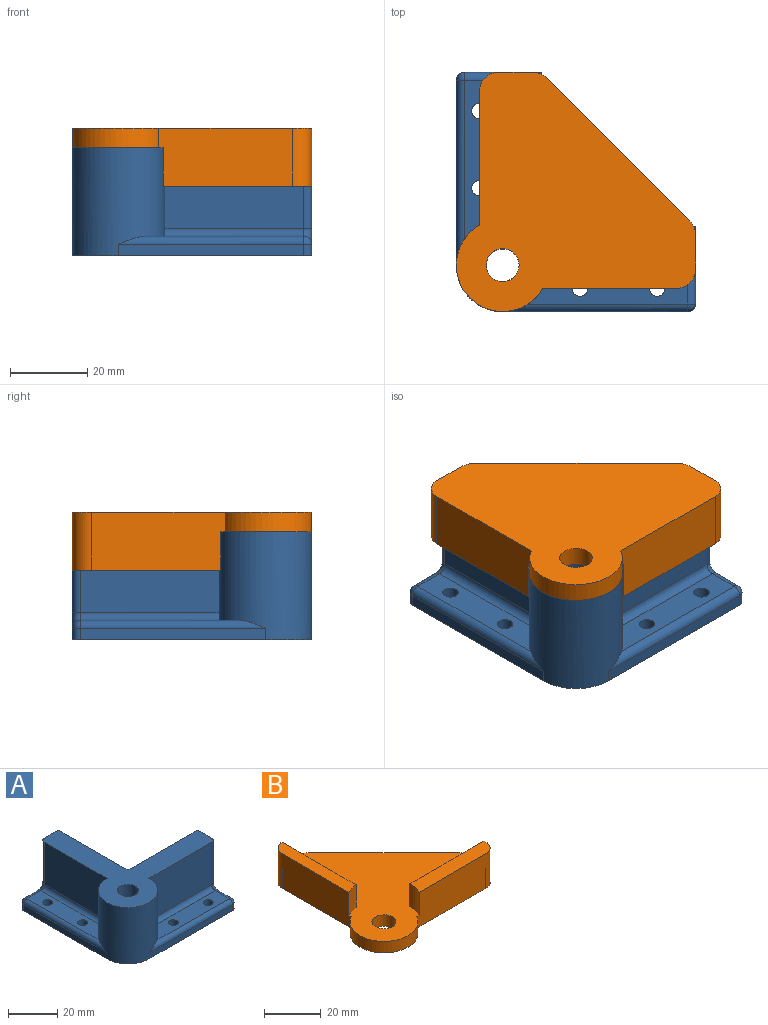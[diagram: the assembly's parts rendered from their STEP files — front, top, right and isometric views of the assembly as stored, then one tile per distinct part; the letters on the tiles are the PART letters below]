
ASSEMBLY  parts=2 mates=1
PART A: 40 faces, bbox 62x62x28 mm
  f0: cylinder r=12mm len=28mm, axis (0,0,-1), area 1404mm2, adj f1,f2,f7,f8,f11,f12,f13,f16
  f1: plane 36x21mm, normal (-1,0,0), area 756mm2, adj f0,f7,f28,f31
  f2: plane 36x21mm, normal (0,-1,0), area 756mm2, adj f0,f7,f32,f33
  f3: plane 28x20mm, normal (1,0,0), area 263.4mm2, adj f4,f7,f8,f33,f34,f36,f38
  f4: plane 38x28mm, normal (0,1,0), area 1064mm2, adj f3,f7,f8,f39
  f5: plane 38x28mm, normal (1,0,0), area 1064mm2, adj f6,f7,f8,f39
  f6: plane 28x20mm, normal (0,1,0), area 263.4mm2, adj f5,f7,f8,f26,f29,f30,f31
  f7: plane 62x62mm, normal (0,0,1), area 1181.7mm2, adj f0,f1,f2,f3,f4,f5,f6,f17
  f8: plane 62x62mm, normal (0,0,-1), area 2015.8mm2, adj f0,f3,f4,f5,f6,f9,f10,f11
  f9: cylinder r=2mm len=5mm, axis (0,0,-1), area 62.8mm2, adj f8,f12
  f10: cylinder r=2mm len=5mm, axis (0,0,-1), area 62.8mm2, adj f8,f12
  f11: plane 48x3mm, normal (-1,0,0), area 144mm2, adj f0,f8,f25,f26
  f12: plane 41.37x8mm, normal (0,0,1), area 278.7mm2, adj f0,f9,f10,f25,f28,f29
  f13: plane 48x3mm, normal (0,-1,0), area 144mm2, adj f0,f8,f35,f38
  f14: cylinder r=2mm len=5mm, axis (0,0,-1), area 62.8mm2, adj f8,f16
  f15: cylinder r=2mm len=5mm, axis (0,0,-1), area 62.8mm2, adj f8,f16
  f16: plane 41.37x8mm, normal (0,0,1), area 278.7mm2, adj f0,f14,f15,f32,f35,f36
  f17: cylinder r=4.25mm len=21mm, axis (0,0,-1), area 560.8mm2, adj f7,f24
  f18: plane 7.26x7mm, normal (-0.25,0.97,0), area 52.5mm2, adj f8,f19,f23,f24
  f19: plane 7.23x7mm, normal (-0.96,0.27,0), area 52.5mm2, adj f8,f18,f20,f24
  f20: plane 7x5.34mm, normal (-0.71,-0.7,0), area 52.5mm2, adj f8,f19,f21,f24
  f21: plane 7.26x7mm, normal (0.25,-0.97,0), area 52.5mm2, adj f8,f20,f22,f24
  f22: plane 7.23x7mm, normal (0.96,-0.27,0), area 52.5mm2, adj f8,f21,f23,f24
  f23: plane 7x5.34mm, normal (0.71,0.7,0), area 52.5mm2, adj f8,f18,f22,f24
  f24: plane 14.52x14.46mm, normal (0,0,-1), area 89.4mm2, adj f17,f18,f19,f20,f21,f22,f23
  f25: cylinder r=2mm len=48mm, axis (0,1,0), area 139.6mm2, adj f0,f11,f12,f27
  f26: cylinder r=2mm len=3mm, axis (0,0,-1), area 9.4mm2, adj f6,f8,f11,f27
  f27: sphere r=2mm, area 6.3mm2, adj f25,f26,f29
  f28: cylinder r=2mm len=36.17mm, axis (0,-1,0), area 113.4mm2, adj f0,f1,f12,f30
  f29: cylinder r=2mm len=8mm, axis (1,0,0), area 25.1mm2, adj f6,f12,f27,f30
  f30: torus R=4mm, axis (0,1,0), area 13.5mm2, adj f6,f28,f29,f31
  f31: cylinder r=2mm len=21mm, axis (0,0,-1), area 66mm2, adj f1,f6,f7,f30
  f32: cylinder r=2mm len=36.17mm, axis (1,0,0), area 113.4mm2, adj f0,f2,f16,f34
  f33: cylinder r=2mm len=21mm, axis (0,0,-1), area 66mm2, adj f2,f3,f7,f34
  f34: torus R=4mm, axis (1,0,0), area 13.5mm2, adj f3,f32,f33,f36
  f35: cylinder r=2mm len=48mm, axis (-1,0,0), area 139.6mm2, adj f0,f13,f16,f37
  f36: cylinder r=2mm len=8mm, axis (0,1,0), area 25.1mm2, adj f3,f16,f34,f37
  f37: sphere r=2mm, area 6.3mm2, adj f35,f36,f38
  f38: cylinder r=2mm len=3mm, axis (0,0,1), area 9.4mm2, adj f3,f8,f13,f37
  f39: cylinder r=2mm len=28mm, axis (0,0,1), area 88mm2, adj f4,f5,f7,f8
PART B: 19 faces, bbox 62x62x15 mm
  f0: plane 15x8.93mm, normal (1,0,0), area 54.6mm2, adj f7,f8,f9,f11,f16,f17
  f1: plane 37.07x37.07mm, normal (0.71,0.71,0), area 262.1mm2, adj f7,f8,f17,f18
  f2: plane 8.93x5mm, normal (0,1,0), area 44.6mm2, adj f7,f8,f15,f18
  f3: plane 34.61x15mm, normal (-1,0,0), area 507.7mm2, adj f4,f7,f8,f12,f14,f15
  f4: cylinder r=12mm len=22.39mm, axis (0,0,-1), area 219.9mm2, adj f3,f5,f7,f8
  f5: plane 34.61x15mm, normal (0,-1,0), area 507.7mm2, adj f4,f7,f8,f10,f11,f16
  f6: cylinder r=4.25mm len=8.5mm, axis (0,0,-1), area 133.5mm2, adj f7,f8
  f7: plane 62x62mm, normal (0,0,1), area 2031mm2, adj f0,f1,f2,f3,f4,f5,f6,f9
  f8: plane 62x62mm, normal (0,0,-1), area 2433mm2, adj f0,f1,f2,f3,f4,f5,f6,f15
  f9: plane 37x10mm, normal (0,1,0), area 370mm2, adj f0,f7,f10,f11
  f10: cylinder r=13mm len=10mm, axis (0,0,-1), area 62.4mm2, adj f5,f7,f9,f11
  f11: plane 38.47x6mm, normal (0,0,1), area 219.5mm2, adj f0,f5,f9,f10,f16
  f12: cylinder r=13mm len=10mm, axis (0,0,-1), area 52.4mm2, adj f3,f7,f13,f14
  f13: plane 37.04x10mm, normal (1,0,0), area 370.4mm2, adj f7,f12,f14,f15
  f14: plane 38.47x5mm, normal (0,0,1), area 182.5mm2, adj f3,f12,f13,f15
  f15: cylinder r=5mm len=15mm, axis (0,0,1), area 117.8mm2, adj f2,f3,f8,f13,f14
  f16: cylinder r=5mm len=15mm, axis (0,0,-1), area 117.8mm2, adj f0,f5,f8,f11
  f17: cylinder r=5mm len=5mm, axis (0,0,-1), area 19.6mm2, adj f0,f1,f7,f8
  f18: cylinder r=5mm len=5mm, axis (0,0,-1), area 19.6mm2, adj f1,f2,f7,f8
PLACE A rot(axis=(0.15,-0.05,0.99),0deg) t=(90.38,101.59,-11.31)mm
PLACE B rot(axis=(-0.71,-0.71,0),180deg) t=(86.47,102.21,21.69)mm
MATE slider A.f0 <-> B.f4  axis (0,0,1) through (77.33,91.59,16.69)mm
